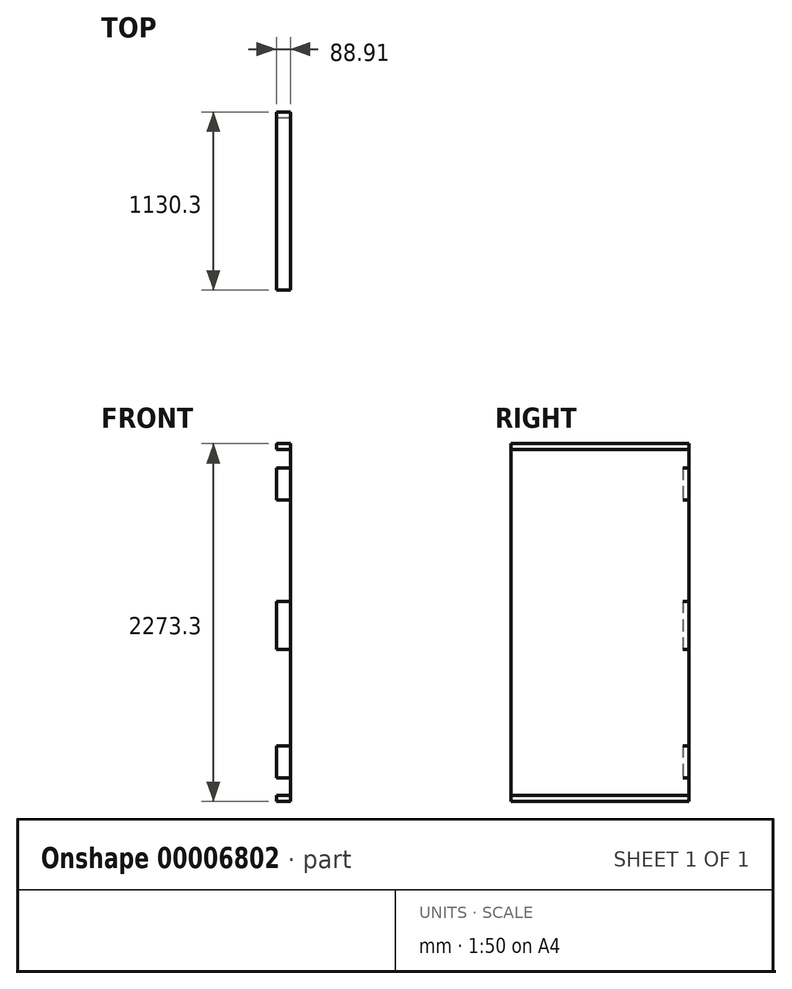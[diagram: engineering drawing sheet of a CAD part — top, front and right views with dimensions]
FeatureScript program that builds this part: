
annotation { "Feature Type Name" : "Feature", "Feature Type Description" : "" }
export const myFeature = defineFeature(function(context is Context, id is Id, definition is map)
    precondition{}
    {
        {
            var Q0;
            Q0=qCreatedBy(makeId("Right.planeOp"),FACE);
            var sketch = newSketch(context, id + "F0", { "sketchPlane" : qUnion([Q0])});
            skLineSegment(sketch, "E0.rect.bottom", {"start": v(565.15, 1136.65) * mm, "end": v(-565.15, 1136.65) * mm, "construction": true});
            skLineSegment(sketch, "E0.rect.top", {"start": v(565.15, -1136.65) * mm, "end": v(-565.15, -1136.65) * mm, "construction": true});
            skLineSegment(sketch, "E0.rect.left", {"start": v(565.15, 1136.65) * mm, "end": v(565.15, -1136.65) * mm, "construction": true});
            skLineSegment(sketch, "E0.rect.right", {"start": v(-565.15, 1136.65) * mm, "end": v(-565.15, -1136.65) * mm, "construction": true});
            skPoint(sketch, "E0.rect.middle", {"position": v(0, 0) * mm});
            skLineSegment(sketch, "E1.bottom", {"start": v(-565.15, 1136.65) * mm, "end": v(565.15, 1136.65) * mm});
            skLineSegment(sketch, "E1.top", {"start": v(-565.15, 1098.55) * mm, "end": v(565.15, 1098.55) * mm});
            skLineSegment(sketch, "E1.left", {"start": v(-565.15, 1136.65) * mm, "end": v(-565.15, 1098.55) * mm});
            skLineSegment(sketch, "E1.right", {"start": v(565.15, 1136.65) * mm, "end": v(565.15, 1098.55) * mm});
            skLineSegment(sketch, "E2", {"start": v(-565.15, 0) * mm, "end": v(565.15, 0) * mm, "construction": true});
            skLineSegment(sketch, "E3.1.MirrorCS", {"start": v(-565.15, -1098.55) * mm, "end": v(565.15, -1098.55) * mm});
            skLineSegment(sketch, "E3.2.MirrorCS", {"start": v(-565.15, -1136.65) * mm, "end": v(-565.15, -1098.55) * mm});
            skLineSegment(sketch, "E3.3.MirrorCS", {"start": v(565.15, -1136.65) * mm, "end": v(565.15, -1098.55) * mm});
            skLineSegment(sketch, "E3.4.MirrorCS", {"start": v(-565.15, -1136.65) * mm, "end": v(565.15, -1136.65) * mm});
            skLineSegment(sketch, "E4.bottom", {"start": v(-565.15, 1098.55) * mm, "end": v(-527.05, 1098.55) * mm});
            skLineSegment(sketch, "E4.top", {"start": v(-565.15, -1098.55) * mm, "end": v(-527.05, -1098.55) * mm});
            skLineSegment(sketch, "E4.left", {"start": v(-565.15, 1098.55) * mm, "end": v(-565.15, -1098.55) * mm});
            skLineSegment(sketch, "E4.right", {"start": v(-527.05, 1098.55) * mm, "end": v(-527.05, -1098.55) * mm});
            skLineSegment(sketch, "E5.0.MirrorCS", {"start": v(565.15, 1098.55) * mm, "end": v(527.05, 1098.55) * mm});
            skLineSegment(sketch, "E5.1.MirrorCS", {"start": v(565.15, -1098.55) * mm, "end": v(527.05, -1098.55) * mm});
            skLineSegment(sketch, "E6.bottom", {"start": v(565.15, 980.75) * mm, "end": v(527.05, 980.75) * mm});
            skLineSegment(sketch, "E6.top", {"start": v(565.15, 777.55) * mm, "end": v(527.05, 777.55) * mm});
            skLineSegment(sketch, "E6.left", {"start": v(565.15, 980.75) * mm, "end": v(565.15, 777.55) * mm});
            skLineSegment(sketch, "E6.right", {"start": v(527.05, 980.75) * mm, "end": v(527.05, 777.55) * mm});
            skLineSegment(sketch, "E7.bottom", {"start": v(565.15, 134.85) * mm, "end": v(527.05, 134.85) * mm});
            skLineSegment(sketch, "E7.top", {"start": v(565.15, -169.95) * mm, "end": v(527.05, -169.95) * mm});
            skLineSegment(sketch, "E7.left", {"start": v(565.15, 134.85) * mm, "end": v(565.15, -169.95) * mm});
            skLineSegment(sketch, "E7.right", {"start": v(527.05, 134.85) * mm, "end": v(527.05, -169.95) * mm});
            skLineSegment(sketch, "E8.bottom", {"start": v(565.15, -783.39) * mm, "end": v(527.05, -783.39) * mm});
            skLineSegment(sketch, "E8.top", {"start": v(565.15, -986.59) * mm, "end": v(527.05, -986.59) * mm});
            skLineSegment(sketch, "E8.left", {"start": v(565.15, -783.39) * mm, "end": v(565.15, -986.59) * mm});
            skLineSegment(sketch, "E8.right", {"start": v(527.05, -783.39) * mm, "end": v(527.05, -986.59) * mm});
            skSolve(sketch);
        }
        {
            var Q0;
            Q0=makeQuery(id+"F0.imprint","IMPRINT",FACE,{"disambiguationData":[TD([[makeQuery(id+"F0.imprint","IMPRINT",EDGE,{"derivedFrom":sQuery(id+"F0.wireOp",EDGE,"E4.bottom")}),-1.0]])]});
            var Q1;
            Q1=makeQuery(id+"F0.imprint","IMPRINT",FACE,{"disambiguationData":[TD([[makeQuery(id+"F0.imprint","IMPRINT",EDGE,{"derivedFrom":sQuery(id+"F0.wireOp",EDGE,"E5.0.MirrorCS")}),1.0]])]});
            var Q2;
            Q2=makeQuery(id+"F0.imprint","IMPRINT",FACE,{"disambiguationData":[TD([[makeQuery(id+"F0.imprint","IMPRINT",EDGE,{"derivedFrom":sQuery(id+"F0.wireOp",EDGE,"E8.bottom")}),1.0]])]});
            var Q3;
            Q3=makeQuery(id+"F0.imprint","IMPRINT",FACE,{"disambiguationData":[TD([[makeQuery(id+"F0.imprint","IMPRINT",EDGE,{"derivedFrom":sQuery(id+"F0.wireOp",EDGE,"E7.bottom")}),1.0]])]});
            var Q4;
            Q4=makeQuery(id+"F0.imprint","IMPRINT",FACE,{"disambiguationData":[TD([[makeQuery(id+"F0.imprint","IMPRINT",EDGE,{"derivedFrom":sQuery(id+"F0.wireOp",EDGE,"E6.bottom")}),1.0]])]});
            extrude(context, id + "F1", {"entities" : qUnion([Q0, Q1, Q2, Q3, Q4]), "depth" : 88.9 * mm});
        }
        {
            var Q0;
            Q0=makeQuery(id+"F0.imprint","IMPRINT",FACE,{"disambiguationData":[TD([[makeQuery(id+"F0.imprint","IMPRINT",EDGE,{"derivedFrom":sQuery(id+"F0.wireOp",EDGE,"E1.bottom")}),-1.0]])]});
            var Q1;
            Q1=makeQuery(id+"F0.imprint","IMPRINT",FACE,{"disambiguationData":[TD([[makeQuery(id+"F0.imprint","IMPRINT",EDGE,{"derivedFrom":sQuery(id+"F0.wireOp",EDGE,"E3.1.MirrorCS")}),-1.0]])]});
            extrude(context, id + "F2", {"entities" : qUnion([Q0, Q1]), "depth" : 88.9 * mm});
        }
        {
            var Q0;
            Q0=makeQuery(id+"F2.opExtrude","CAP_FACE",FACE,{"disambiguationData":[OSD([sQuery(id+"F0.wireOp",EDGE,"E1.bottom"),sQuery(id+"F0.wireOp",EDGE,"E1.top"),sQuery(id+"F0.wireOp",EDGE,"E1.left"),sQuery(id+"F0.wireOp",EDGE,"E1.right"),sQuery(id+"F0.wireOp",EDGE,"E4.bottom"),sQuery(id+"F0.wireOp",EDGE,"E5.0.MirrorCS")])],"isStart":false});
            var sketch = newSketch(context, id + "F3", { "sketchPlane" : qUnion([Q0])});
            skPoint(sketch, "E9.0", {"position": v(-565.15, 1136.65) * mm});
            skPoint(sketch, "E10.0", {"position": v(565.15, -1136.65) * mm});
            skLineSegment(sketch, "E11.bottom", {"start": v(-565.15, 1136.65) * mm, "end": v(565.15, 1136.65) * mm});
            skLineSegment(sketch, "E11.top", {"start": v(-565.15, -1136.65) * mm, "end": v(565.15, -1136.65) * mm});
            skLineSegment(sketch, "E11.left", {"start": v(-565.15, 1136.65) * mm, "end": v(-565.15, -1136.65) * mm});
            skLineSegment(sketch, "E11.right", {"start": v(565.15, 1136.65) * mm, "end": v(565.15, -1136.65) * mm});
            skSolve(sketch);
        }
        {
            var Q0;
            Q0 = qSketchRegion(id + "F3", true);
            extrude(context, id + "F4", {"entities" : qUnion([Q0]), "depth" : 3 / 203.2 * mm});
        }
    });
